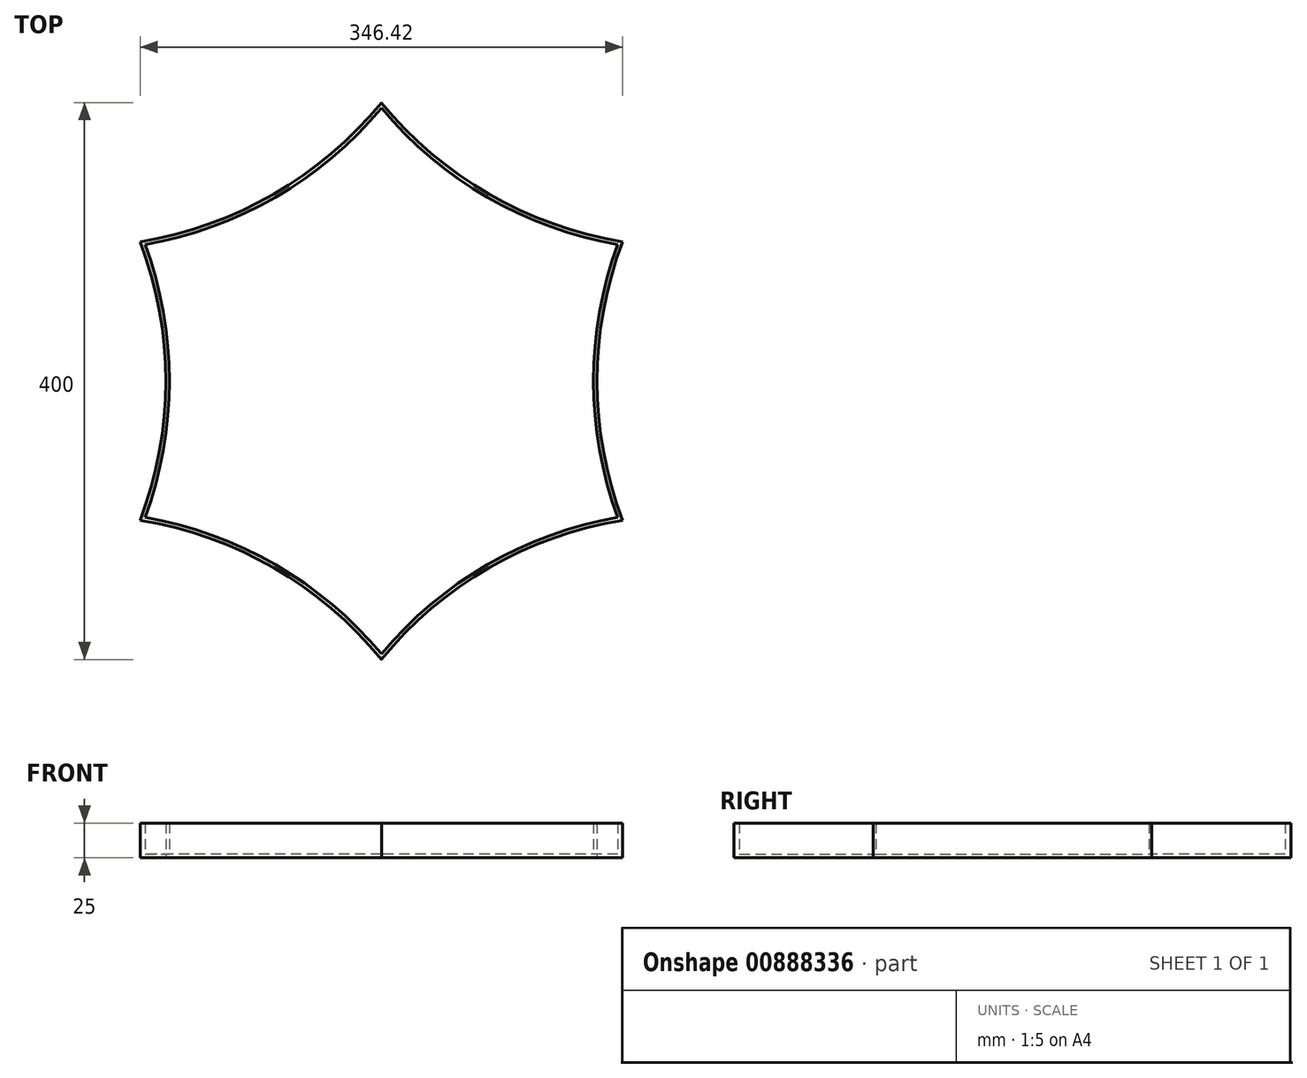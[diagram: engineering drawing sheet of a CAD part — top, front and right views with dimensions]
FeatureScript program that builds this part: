
annotation { "Feature Type Name" : "Feature", "Feature Type Description" : "" }
export const myFeature = defineFeature(function(context is Context, id is Id, definition is map)
    precondition{}
    {
        {
            var Q0;
            Q0=qCreatedBy(makeId("Top.planeOp"),FACE);
            var sketch = newSketch(context, id + "F0", { "sketchPlane" : qUnion([Q0])});
            skArc(sketch, "E0", {"start": v(-173.2, -100) * mm, "mid": v(-154.86, 0) * mm, "end": v(-173.2, 100) * mm});
            skArc(sketch, "E1.1.0", {"start": v(0, -200) * mm, "mid": v(-77.43, -134.11) * mm, "end": v(-173.2, -100) * mm});
            skArc(sketch, "E1.2.0", {"start": v(173.2, -100) * mm, "mid": v(77.43, -134.11) * mm, "end": v(0, -200) * mm});
            skArc(sketch, "E1.3.0", {"start": v(173.2, 100) * mm, "mid": v(154.86, 0) * mm, "end": v(173.2, -100) * mm});
            skArc(sketch, "E1.4.0", {"start": v(0, 200) * mm, "mid": v(77.43, 134.11) * mm, "end": v(173.2, 100) * mm});
            skArc(sketch, "E1.5.0", {"start": v(-173.2, 100) * mm, "mid": v(-77.43, 134.11) * mm, "end": v(0, 200) * mm});
            skPoint(sketch, "E1.center", {"position": v(0, 0) * mm});
            skSolve(sketch);
        }
        {
            var Q0;
            Q0 = qSketchRegion(id + "F0", true);
            extrude(context, id + "F1", {"entities" : qUnion([Q0]), "depth" : 25 * mm, "offsetDistance" : 25 * mm});
        }
        {
            var Q0;
            Q0=makeQuery(id+"F1.opExtrude","CAP_FACE",FACE,{"disambiguationData":[OSD([sQuery(id+"F0.wireOp",EDGE,"E0"),sQuery(id+"F0.wireOp",EDGE,"E1.1.0"),sQuery(id+"F0.wireOp",EDGE,"E1.2.0"),sQuery(id+"F0.wireOp",EDGE,"E1.3.0"),sQuery(id+"F0.wireOp",EDGE,"E1.4.0"),sQuery(id+"F0.wireOp",EDGE,"E1.5.0")])],"isStart":false});
            shell(context, id + "F2", {"entities" : qUnion([Q0]), "thickness" : 2.5 * mm});
        }
    });
